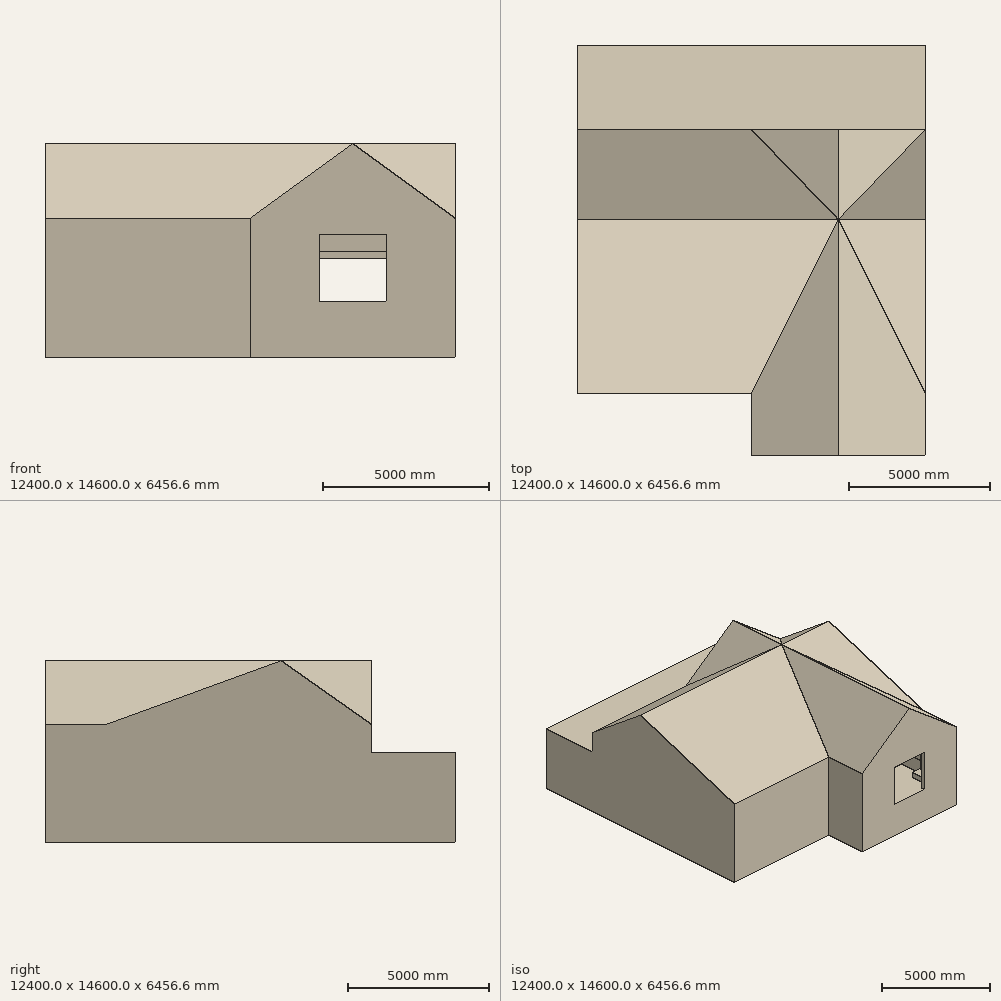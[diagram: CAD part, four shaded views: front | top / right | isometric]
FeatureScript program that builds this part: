
annotation { "Feature Type Name" : "Feature", "Feature Type Description" : "" }
export const myFeature = defineFeature(function(context is Context, id is Id, definition is map)
    precondition{}
    {
        {
            var Q0;
            Q0=qCreatedBy(makeId("Right.planeOp"),FACE);
            var sketch = newSketch(context, id + "F13", { "sketchPlane" : qUnion([Q0])});
            skLineSegment(sketch, "E0", {"start": v(6200, 0) * mm, "end": v(-6200, 0) * mm});
            skLineSegment(sketch, "E1", {"start": v(-6200, 0) * mm, "end": v(-6200, 4000) * mm});
            skLineSegment(sketch, "E2", {"start": v(-6200, 4000) * mm, "end": v(0, 6256.62) * mm});
            skLineSegment(sketch, "E3", {"start": v(0, 6256.62) * mm, "end": v(3200, 4000) * mm});
            skLineSegment(sketch, "E4", {"start": v(3200, 4000) * mm, "end": v(3200, 3000) * mm});
            skLineSegment(sketch, "E5", {"start": v(3200, 3000) * mm, "end": v(6200, 3000) * mm});
            skLineSegment(sketch, "E6", {"start": v(6200, 3000) * mm, "end": v(6200, 0) * mm});
            skLineSegment(sketch, "E7", {"start": v(-6200, 4000) * mm, "end": v(3200, 4000) * mm, "construction": true});
            skLineSegment(sketch, "E8", {"start": v(0, 6256.62) * mm, "end": v(0, 0) * mm, "construction": true});
            skSolve(sketch);
        }
        {
            var Q0;
            Q0 = qSketchRegion(id + "F13", true);
            extrude(context, id + "F14", {"entities" : qUnion([Q0]), "depth" : 12400 * mm});
        }
        {
            var Q0;
            Q0=makeQuery(id+"F14.opExtrude","SWEPT_FACE",FACE,{"disambiguationData":[OSD([sQuery(id+"F13.wireOp",EDGE,"E4")])]});
            var sketch = newSketch(context, id + "F15", { "sketchPlane" : qUnion([Q0])});
            skLineSegment(sketch, "E9", {"start": v(-12400, 4000) * mm, "end": v(-9300, 6256.62) * mm});
            skLineSegment(sketch, "E10", {"start": v(-9300, 6256.62) * mm, "end": v(-6200, 4000) * mm});
            skLineSegment(sketch, "E11", {"start": v(-6200, 4000) * mm, "end": v(-6200, 3000) * mm});
            skLineSegment(sketch, "E12", {"start": v(-6200, 3000) * mm, "end": v(-12400, 3000) * mm});
            skLineSegment(sketch, "E13", {"start": v(-12400, 4000) * mm, "end": v(-12400, 3000) * mm});
            skLineSegment(sketch, "E14", {"start": v(-9300, 6256.62) * mm, "end": v(-9300, 3000) * mm, "construction": true});
            skLineSegment(sketch, "E15", {"start": v(-12400, 5500) * mm, "end": v(-6200, 5500) * mm, "construction": true});
            skLineSegment(sketch, "E16", {"start": v(-12400, 4000) * mm, "end": v(-6200, 4000) * mm});
            skLineSegment(sketch, "E17.bottom", {"start": v(-10300, 3000) * mm, "end": v(-8300, 3000) * mm});
            skLineSegment(sketch, "E17.top", {"start": v(-10300, 5000) * mm, "end": v(-8300, 5000) * mm});
            skLineSegment(sketch, "E17.left", {"start": v(-10300, 3000) * mm, "end": v(-10300, 5000) * mm});
            skLineSegment(sketch, "E17.right", {"start": v(-8300, 3000) * mm, "end": v(-8300, 5000) * mm});
            skSolve(sketch);
        }
        {
            var Q0;
            Q0=makeQuery(id+"F15.imprint","IMPRINT",FACE,{"disambiguationData":[TD([[makeQuery(id+"F15.imprint","IMPRINT",EDGE,{"derivedFrom":sQuery(id+"F15.wireOp",EDGE,"E9")}),-1.0]])]});
            var Q1;
            {var subQ5=sQuery(id+"F15.wireOp",EDGE,"E17.top");Q1=makeQuery(id+"F15.imprint","IMPRINT",FACE,{"disambiguationData":[TD([[makeQuery(id+"F15.imprint","IMPRINT",EDGE,{"derivedFrom":subQ5}),-1.0]])]});}
            var Q2;
            Q2=makeQuery(id+"F14.opExtrude","SWEPT_FACE",FACE,{"disambiguationData":[OSD([sQuery(id+"F13.wireOp",EDGE,"E1")])]});
            extrude(context, id + "F0", {"entities" : qUnion([Q0, Q1]), "operationType" : NewBodyOperationType.ADD, "oppositeDirection" : true, "endBoundEntityFace" : qUnion([Q2]), "depth" : 11600 * mm});
        }
        {
            var Q0;
            Q0=makeQuery(id+"F0.opExtrude","SWEPT_FACE",FACE,{"disambiguationData":[OSD([sQuery(id+"F15.wireOp",EDGE,"E16")])]});
            var Q1;
            Q1=makeQuery(id+"F14.opExtrude","SWEPT_FACE",FACE,{"disambiguationData":[OSD([sQuery(id+"F13.wireOp",EDGE,"E0")])]});
            extrude(context, id + "F16", {"entities" : qUnion([Q0]), "operationType" : NewBodyOperationType.ADD, "endBound" : BoundingType.UP_TO_SURFACE, "endBoundEntityFace" : qUnion([Q1]), "depth" : 25 * mm});
        }
        {
            var Q0;
            Q0=makeQuery(id+"F16.boolean.opBoolean","MERGE",FACE,{"derivedFrom":[makeQuery(id+"F14.opExtrude","SWEPT_FACE",FACE,{"disambiguationData":[OSD([sQuery(id+"F13.wireOp",EDGE,"E0")])]}),makeQuery(id+"F16.opExtrude","CAP_FACE",FACE,{"disambiguationData":[OSD([sQuery(id+"F15.wireOp",EDGE,"E16")])],"isStart":false})]});
            var Q1;
            Q1=makeQuery(id+"F14.opExtrude","SWEPT_FACE",FACE,{"disambiguationData":[OSD([sQuery(id+"F13.wireOp",EDGE,"E6")])]});
            var Q2;
            Q2=makeQuery(id+"F14.opExtrude","SWEPT_FACE",FACE,{"disambiguationData":[OSD([sQuery(id+"F13.wireOp",EDGE,"E5")])]});
            shell(context, id + "F1", {"entities" : qUnion([Q0, Q1, Q2]), "thickness" : 200 * mm});
        }
        {
            var Q0;
            {var subQ0=sQuery(id+"F15.wireOp",EDGE,"E16");Q0=makeQuery(id+"F16.boolean.opBoolean","MERGE",FACE,{"derivedFrom":[makeQuery(id+"F0.opExtrude","CAP_FACE",FACE,{"disambiguationData":[OSD([sQuery(id+"F15.wireOp",EDGE,"E9"),sQuery(id+"F15.wireOp",EDGE,"E10"),subQ0])],"isStart":false}),makeQuery(id+"F16.opExtrude","SWEPT_FACE",FACE,{"disambiguationData":[OSD([subQ0])]})]});}
            var sketch = newSketch(context, id + "F2", { "sketchPlane" : qUnion([Q0])});
            skLineSegment(sketch, "E18.bottom", {"start": v(8300, 1500) * mm, "end": v(10300, 1500) * mm});
            skLineSegment(sketch, "E18.top", {"start": v(8300, 3500) * mm, "end": v(10300, 3500) * mm});
            skLineSegment(sketch, "E18.left", {"start": v(8300, 1500) * mm, "end": v(8300, 3500) * mm});
            skLineSegment(sketch, "E18.right", {"start": v(10300, 1500) * mm, "end": v(10300, 3500) * mm});
            skLineSegment(sketch, "E19", {"start": v(9300, 6256.62) * mm, "end": v(9300, 0) * mm, "construction": true});
            skPoint(sketch, "E20", {"position": v(9300, 1500) * mm});
            skSolve(sketch);
        }
        {
            var Q0;
            Q0=makeQuery(id+"F2.imprint","IMPRINT",FACE,{"disambiguationData":[TD([[makeQuery(id+"F2.imprint","IMPRINT",EDGE,{"derivedFrom":sQuery(id+"F2.wireOp",EDGE,"E18.bottom")}),1.0]])]});
            var Q1;
            Q1=makeQuery(id+"F1.opShell","OFFSET_FACE",FACE,{"disambiguationData":[OSD([sQuery(id+"F15.wireOp",EDGE,"E9"),sQuery(id+"F15.wireOp",EDGE,"E10"),sQuery(id+"F15.wireOp",EDGE,"E16")])]});
            extrude(context, id + "F17", {"entities" : qUnion([Q0]), "operationType" : NewBodyOperationType.REMOVE, "endBound" : BoundingType.UP_TO_SURFACE, "oppositeDirection" : true, "endBoundEntityFace" : qUnion([Q1]), "depth" : 25 * mm});
        }
        {
            var Q0;
            {var subQ5=sQuery(id+"F15.wireOp",EDGE,"E17.bottom");Q0=makeQuery(id+"F15.imprint","IMPRINT",FACE,{"disambiguationData":[TD([[makeQuery(id+"F15.imprint","IMPRINT",EDGE,{"derivedFrom":subQ5}),1.0]])]});}
            var Q1;
            {var subQ5=sQuery(id+"F15.wireOp",EDGE,"E17.top");Q1=makeQuery(id+"F15.imprint","IMPRINT",FACE,{"disambiguationData":[TD([[makeQuery(id+"F15.imprint","IMPRINT",EDGE,{"derivedFrom":subQ5}),-1.0]])]});}
            var Q2;
            Q2=makeQuery(id+"F1.opShell","OFFSET_FACE",FACE,{"disambiguationData":[OSD([sQuery(id+"F13.wireOp",EDGE,"E4"),sQuery(id+"F15.wireOp",EDGE,"E9"),sQuery(id+"F15.wireOp",EDGE,"E10"),sQuery(id+"F15.wireOp",EDGE,"E16")])]});
            extrude(context, id + "F18", {"entities" : qUnion([Q0, Q1]), "operationType" : NewBodyOperationType.REMOVE, "endBound" : BoundingType.UP_TO_SURFACE, "oppositeDirection" : true, "endBoundEntityFace" : qUnion([Q2]), "depth" : 25 * mm});
        }
        {
            var Q0;
            Q0=makeQuery(id+"F16.boolean.opBoolean","MERGE",FACE,{"derivedFrom":[makeQuery(id+"F14.opExtrude","SWEPT_FACE",FACE,{"disambiguationData":[OSD([sQuery(id+"F13.wireOp",EDGE,"E0")])]}),makeQuery(id+"F16.opExtrude","CAP_FACE",FACE,{"disambiguationData":[OSD([sQuery(id+"F15.wireOp",EDGE,"E16")])],"isStart":false})]});
            var sketch = newSketch(context, id + "F3", { "sketchPlane" : qUnion([Q0])});
            skLineSegment(sketch, "E21", {"start": v(6400, 6000) * mm, "end": v(6400, 8200) * mm});
            skLineSegment(sketch, "E22", {"start": v(6400, 8200) * mm, "end": v(12200, 8200) * mm});
            skLineSegment(sketch, "E23", {"start": v(6400, 6000) * mm, "end": v(12200, 6000) * mm});
            skLineSegment(sketch, "E24", {"start": v(12200, 6000) * mm, "end": v(12200, 8200) * mm});
            skLineSegment(sketch, "E25", {"start": v(12400, 8400) * mm, "end": v(12400, -6200) * mm});
            skLineSegment(sketch, "E26", {"start": v(12400, -6200) * mm, "end": v(0, -6200) * mm});
            skLineSegment(sketch, "E27", {"start": v(0, -6200) * mm, "end": v(0, 6200) * mm});
            skLineSegment(sketch, "E28", {"start": v(0, 6200) * mm, "end": v(6200, 6200) * mm});
            skLineSegment(sketch, "E29", {"start": v(6200, 6200) * mm, "end": v(6200, 8400) * mm});
            skLineSegment(sketch, "E30", {"start": v(6200, 8400) * mm, "end": v(12400, 8400) * mm});
            skLineSegment(sketch, "E31", {"start": v(12200, 6000) * mm, "end": v(12200, -6200) * mm});
            skLineSegment(sketch, "E32", {"start": v(6400, 6000) * mm, "end": v(200, 6000) * mm});
            skLineSegment(sketch, "E33", {"start": v(200, 6000) * mm, "end": v(200, -6200) * mm});
            skLineSegment(sketch, "E34", {"start": v(9300, 8200) * mm, "end": v(9300, 6000) * mm, "construction": true});
            skLineSegment(sketch, "E35", {"start": v(7900, 8200) * mm, "end": v(7900, 7200) * mm});
            skLineSegment(sketch, "E36", {"start": v(7400, 8200) * mm, "end": v(7400, 6000) * mm});
            skLineSegment(sketch, "E37", {"start": v(6400, 6700) * mm, "end": v(7400, 6700) * mm});
            skLineSegment(sketch, "E38", {"start": v(6400, 7200) * mm, "end": v(7400, 7200) * mm});
            skLineSegment(sketch, "E39", {"start": v(6400, 6200) * mm, "end": v(7400, 6200) * mm});
            skLineSegment(sketch, "E40", {"start": v(7400, 7200) * mm, "end": v(7900, 7200) * mm});
            skLineSegment(sketch, "E41", {"start": v(7400, 7200) * mm, "end": v(6400, 8200) * mm});
            skLineSegment(sketch, "E42.MirrorCS", {"start": v(10700, 8200) * mm, "end": v(10700, 7200) * mm});
            skLineSegment(sketch, "E43.MirrorCS", {"start": v(11200, 8200) * mm, "end": v(11200, 6000) * mm});
            skLineSegment(sketch, "E44.MirrorCS", {"start": v(11200, 7200) * mm, "end": v(12200, 8200) * mm});
            skLineSegment(sketch, "E45.MirrorCS", {"start": v(12200, 7200) * mm, "end": v(11200, 7200) * mm});
            skLineSegment(sketch, "E46.MirrorCS", {"start": v(12200, 6700) * mm, "end": v(11200, 6700) * mm});
            skLineSegment(sketch, "E47.MirrorCS", {"start": v(12200, 6200) * mm, "end": v(11200, 6200) * mm});
            skLineSegment(sketch, "E48.MirrorCS", {"start": v(11200, 7200) * mm, "end": v(10700, 7200) * mm});
            skSolve(sketch);
        }
        {
            var Q0;
            Q0 = qSketchRegion(id + "F3", true);
            var Q1;
            {var subQ2=sQuery(id+"F3.wireOp",EDGE,"E38");Q1=makeQuery(id+"F3.imprint","IMPRINT",FACE,{"disambiguationData":[TD([[makeQuery(id+"F3.imprint","IMPRINT",EDGE,{"derivedFrom":subQ2}),1.0]])]});}
            var Q2;
            {var subQ0=sQuery(id+"F3.wireOp",EDGE,"E37");Q2=makeQuery(id+"F3.imprint","IMPRINT",FACE,{"disambiguationData":[TD([[makeQuery(id+"F3.imprint","IMPRINT",EDGE,{"derivedFrom":subQ0}),1.0]])]});}
            var Q3;
            {var subQ0=sQuery(id+"F3.wireOp",EDGE,"E41");Q3=makeQuery(id+"F3.imprint","IMPRINT",FACE,{"disambiguationData":[TD([[makeQuery(id+"F3.imprint","IMPRINT",EDGE,{"derivedFrom":subQ0}),-1.0]])]});}
            var Q4;
            {var subQ0=sQuery(id+"F3.wireOp",EDGE,"E35");Q4=makeQuery(id+"F3.imprint","IMPRINT",FACE,{"disambiguationData":[TD([[makeQuery(id+"F3.imprint","IMPRINT",EDGE,{"derivedFrom":subQ0}),-1.0]])]});}
            var Q5;
            {var subQ12=sQuery(id+"F3.wireOp",EDGE,"E35");Q5=makeQuery(id+"F3.imprint","IMPRINT",FACE,{"disambiguationData":[TD([[makeQuery(id+"F3.imprint","IMPRINT",EDGE,{"derivedFrom":subQ12}),1.0]])]});}
            var Q6;
            {var subQ0=sQuery(id+"F3.wireOp",EDGE,"E37");Q6=makeQuery(id+"F3.imprint","IMPRINT",FACE,{"disambiguationData":[TD([[makeQuery(id+"F3.imprint","IMPRINT",EDGE,{"derivedFrom":subQ0}),-1.0]])]});}
            var Q7;
            {var subQ3=sQuery(id+"F3.wireOp",EDGE,"E39");Q7=makeQuery(id+"F3.imprint","IMPRINT",FACE,{"disambiguationData":[TD([[makeQuery(id+"F3.imprint","IMPRINT",EDGE,{"derivedFrom":subQ3}),-1.0]])]});}
            var Q8;
            {var subQ5=sQuery(id+"F3.wireOp",EDGE,"E47.MirrorCS");Q8=makeQuery(id+"F3.imprint","IMPRINT",FACE,{"disambiguationData":[TD([[makeQuery(id+"F3.imprint","IMPRINT",EDGE,{"derivedFrom":subQ5}),1.0]])]});}
            var Q9;
            {var subQ0=sQuery(id+"F3.wireOp",EDGE,"E46.MirrorCS");Q9=makeQuery(id+"F3.imprint","IMPRINT",FACE,{"disambiguationData":[TD([[makeQuery(id+"F3.imprint","IMPRINT",EDGE,{"derivedFrom":subQ0}),1.0]])]});}
            var Q10;
            {var subQ0=sQuery(id+"F3.wireOp",EDGE,"E45.MirrorCS");Q10=makeQuery(id+"F3.imprint","IMPRINT",FACE,{"disambiguationData":[TD([[makeQuery(id+"F3.imprint","IMPRINT",EDGE,{"derivedFrom":subQ0}),1.0]])]});}
            var Q11;
            {var subQ0=sQuery(id+"F3.wireOp",EDGE,"E44.MirrorCS");Q11=makeQuery(id+"F3.imprint","IMPRINT",FACE,{"disambiguationData":[TD([[makeQuery(id+"F3.imprint","IMPRINT",EDGE,{"derivedFrom":subQ0}),-1.0]])]});}
            var Q12;
            {var subQ0=sQuery(id+"F3.wireOp",EDGE,"E44.MirrorCS");Q12=makeQuery(id+"F3.imprint","IMPRINT",FACE,{"disambiguationData":[TD([[makeQuery(id+"F3.imprint","IMPRINT",EDGE,{"derivedFrom":subQ0}),1.0]])]});}
            var Q13;
            {var subQ0=sQuery(id+"F3.wireOp",EDGE,"E42.MirrorCS");Q13=makeQuery(id+"F3.imprint","IMPRINT",FACE,{"disambiguationData":[TD([[makeQuery(id+"F3.imprint","IMPRINT",EDGE,{"derivedFrom":subQ0}),1.0]])]});}
            extrude(context, id + "F4", {"entities" : qUnion([Q0, Q1, Q2, Q3, Q4, Q5, Q6, Q7, Q8, Q9, Q10, Q11, Q12, Q13]), "depth" : 200 * mm});
        }
        {
            var Q0;
            Q0=makeQuery(id+"F3.imprint","IMPRINT",FACE,{"disambiguationData":[TD([[makeQuery(id+"F3.imprint","IMPRINT",EDGE,{"derivedFrom":sQuery(id+"F3.wireOp",EDGE,"E23")}),-1.0]])]});
            extrude(context, id + "F5", {"entities" : qUnion([Q0]), "oppositeDirection" : true, "depth" : 3000 * mm, "hasSecondDirection" : true, "secondDirectionOppositeDirection" : true, "secondDirectionDepth" : 2800 * mm});
        }
        {
            var Q0;
            {var subQ12=sQuery(id+"F3.wireOp",EDGE,"E35");Q0=makeQuery(id+"F3.imprint","IMPRINT",FACE,{"disambiguationData":[TD([[makeQuery(id+"F3.imprint","IMPRINT",EDGE,{"derivedFrom":subQ12}),1.0]])]});}
            extrude(context, id + "F6", {"entities" : qUnion([Q0]), "oppositeDirection" : true, "depth" : 1500 * mm, "hasSecondDirection" : true, "secondDirectionOppositeDirection" : true, "secondDirectionDepth" : 1200 * mm});
        }
        {
            var Q0;
            {var subQ0=sQuery(id+"F3.wireOp",EDGE,"E42.MirrorCS");Q0=makeQuery(id+"F3.imprint","IMPRINT",FACE,{"disambiguationData":[TD([[makeQuery(id+"F3.imprint","IMPRINT",EDGE,{"derivedFrom":subQ0}),1.0]])]});}
            extrude(context, id + "F7", {"entities" : qUnion([Q0]), "operationType" : NewBodyOperationType.ADD, "oppositeDirection" : true, "depth" : 1750 * mm, "hasSecondDirection" : true, "secondDirectionOppositeDirection" : true, "secondDirectionDepth" : 1450 * mm});
        }
        {
            var Q0;
            {var subQ0=sQuery(id+"F3.wireOp",EDGE,"E44.MirrorCS");Q0=makeQuery(id+"F3.imprint","IMPRINT",FACE,{"disambiguationData":[TD([[makeQuery(id+"F3.imprint","IMPRINT",EDGE,{"derivedFrom":subQ0}),1.0]])]});}
            extrude(context, id + "F19", {"entities" : qUnion([Q0]), "operationType" : NewBodyOperationType.ADD, "oppositeDirection" : true, "depth" : 2000 * mm, "hasSecondDirection" : true, "secondDirectionOppositeDirection" : true, "secondDirectionDepth" : 1700 * mm});
        }
        {
            var Q0;
            {var subQ0=sQuery(id+"F3.wireOp",EDGE,"E44.MirrorCS");Q0=makeQuery(id+"F3.imprint","IMPRINT",FACE,{"disambiguationData":[TD([[makeQuery(id+"F3.imprint","IMPRINT",EDGE,{"derivedFrom":subQ0}),-1.0]])]});}
            extrude(context, id + "F20", {"entities" : qUnion([Q0]), "operationType" : NewBodyOperationType.ADD, "oppositeDirection" : true, "depth" : 2250 * mm, "hasSecondDirection" : true, "secondDirectionOppositeDirection" : true, "secondDirectionDepth" : 1950 * mm});
        }
        {
            var Q0;
            {var subQ0=sQuery(id+"F3.wireOp",EDGE,"E45.MirrorCS");Q0=makeQuery(id+"F3.imprint","IMPRINT",FACE,{"disambiguationData":[TD([[makeQuery(id+"F3.imprint","IMPRINT",EDGE,{"derivedFrom":subQ0}),1.0]])]});}
            extrude(context, id + "F21", {"entities" : qUnion([Q0]), "operationType" : NewBodyOperationType.ADD, "oppositeDirection" : true, "depth" : 2500 * mm, "hasSecondDirection" : true, "secondDirectionOppositeDirection" : true, "secondDirectionDepth" : 2200 * mm});
        }
        {
            var Q0;
            {var subQ0=sQuery(id+"F3.wireOp",EDGE,"E46.MirrorCS");Q0=makeQuery(id+"F3.imprint","IMPRINT",FACE,{"disambiguationData":[TD([[makeQuery(id+"F3.imprint","IMPRINT",EDGE,{"derivedFrom":subQ0}),1.0]])]});}
            extrude(context, id + "F8", {"entities" : qUnion([Q0]), "operationType" : NewBodyOperationType.ADD, "oppositeDirection" : true, "depth" : 2750 * mm, "hasSecondDirection" : true, "secondDirectionOppositeDirection" : true, "secondDirectionDepth" : 2450 * mm});
        }
        {
            var Q0;
            {var subQ5=sQuery(id+"F3.wireOp",EDGE,"E47.MirrorCS");Q0=makeQuery(id+"F3.imprint","IMPRINT",FACE,{"disambiguationData":[TD([[makeQuery(id+"F3.imprint","IMPRINT",EDGE,{"derivedFrom":subQ5}),1.0]])]});}
            extrude(context, id + "F22", {"entities" : qUnion([Q0]), "operationType" : NewBodyOperationType.ADD, "oppositeDirection" : true, "depth" : 3000 * mm, "hasSecondDirection" : true, "secondDirectionOppositeDirection" : true, "secondDirectionDepth" : 2700 * mm});
        }
        {
            var Q0;
            {var subQ0=sQuery(id+"F3.wireOp",EDGE,"E35");Q0=makeQuery(id+"F3.imprint","IMPRINT",FACE,{"disambiguationData":[TD([[makeQuery(id+"F3.imprint","IMPRINT",EDGE,{"derivedFrom":subQ0}),-1.0]])]});}
            extrude(context, id + "F9", {"entities" : qUnion([Q0]), "operationType" : NewBodyOperationType.ADD, "oppositeDirection" : true, "depth" : 1250 * mm, "hasSecondDirection" : true, "secondDirectionOppositeDirection" : true, "secondDirectionDepth" : 950 * mm});
        }
        {
            var Q0;
            {var subQ0=sQuery(id+"F3.wireOp",EDGE,"E41");Q0=makeQuery(id+"F3.imprint","IMPRINT",FACE,{"disambiguationData":[TD([[makeQuery(id+"F3.imprint","IMPRINT",EDGE,{"derivedFrom":subQ0}),-1.0]])]});}
            extrude(context, id + "F10", {"entities" : qUnion([Q0]), "operationType" : NewBodyOperationType.ADD, "oppositeDirection" : true, "depth" : 1000 * mm, "hasSecondDirection" : true, "secondDirectionOppositeDirection" : true, "secondDirectionDepth" : 700 * mm});
        }
        {
            var Q0;
            {var subQ2=sQuery(id+"F3.wireOp",EDGE,"E38");Q0=makeQuery(id+"F3.imprint","IMPRINT",FACE,{"disambiguationData":[TD([[makeQuery(id+"F3.imprint","IMPRINT",EDGE,{"derivedFrom":subQ2}),1.0]])]});}
            extrude(context, id + "F11", {"entities" : qUnion([Q0]), "operationType" : NewBodyOperationType.ADD, "oppositeDirection" : true, "depth" : 750 * mm, "hasSecondDirection" : true, "secondDirectionOppositeDirection" : true, "secondDirectionDepth" : 450 * mm});
        }
        {
            var Q0;
            {var subQ0=sQuery(id+"F3.wireOp",EDGE,"E37");Q0=makeQuery(id+"F3.imprint","IMPRINT",FACE,{"disambiguationData":[TD([[makeQuery(id+"F3.imprint","IMPRINT",EDGE,{"derivedFrom":subQ0}),1.0]])]});}
            extrude(context, id + "F23", {"entities" : qUnion([Q0]), "operationType" : NewBodyOperationType.ADD, "oppositeDirection" : true, "depth" : 500 * mm, "hasSecondDirection" : true, "secondDirectionOppositeDirection" : true, "secondDirectionDepth" : 200 * mm});
        }
        {
            var Q0;
            {var subQ0=sQuery(id+"F3.wireOp",EDGE,"E37");Q0=makeQuery(id+"F3.imprint","IMPRINT",FACE,{"disambiguationData":[TD([[makeQuery(id+"F3.imprint","IMPRINT",EDGE,{"derivedFrom":subQ0}),-1.0]])]});}
            extrude(context, id + "F12", {"entities" : qUnion([Q0]), "operationType" : NewBodyOperationType.ADD, "oppositeDirection" : true, "depth" : 250 * mm});
        }
    });
